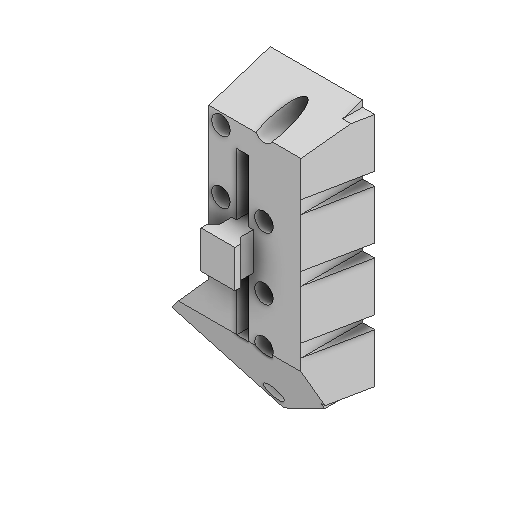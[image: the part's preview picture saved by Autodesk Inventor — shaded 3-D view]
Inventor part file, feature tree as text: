
AUTODESK INVENTOR PART (.ipt)
format: ipt  version: 2025.1 (Build 291241020, 241B)  size: 390,656 bytes
history: native  units: in
note: dims shown in document units (in); Inventor stores cm internally (conversion verified against a paired STEP export)
features: reference x48, other x12, extrude x11, sketch x11, plane x2, chamfer x2, projected_geometry x1
ambient origin geometry x8: Origin, YZ Plane, XZ Plane, XY Plane, X Axis, Y Axis, Z Axis, Center Point
bodies: Solid1 (feature_tree)
feature tree (87):
  extrude  "Extrusion1"  Depth=0.25in TaperAngle=0.0deg
  extrude  "Extrusion2"  Depth=0.14in
  extrude  "Extrusion3"  Depth=0.14in
  plane  "Work Plane1"
  extrude  "Extrusion4"  Depth=0.14in
  extrude  "Extrusion5"  Depth=0.25in TaperAngle=0.0deg
  extrude  "Extrusion6"  Depth=0.3in
  plane  "Work Plane2"
  extrude  "Extrusion7"  Depth=0.3in
  extrude  "Extrusion9"  Depth=0.25in TaperAngle=0.0deg
  extrude  "Extrusion14"  Depth=0.7in
  chamfer  "Chamfer2"  Distance=0.14in
  extrude  "Extrusion15"  Depth=0.25in
  extrude  "Extrusion16"  Depth=0.1in
  chamfer  "Chamfer3"  Distance=0.14in
  sketch  "Sketch1"  dims[d0=0.25in d1=0.0in d2=0.25in d3=0.0in]
  reference  "Reference1"
  reference  "Reference2"
  reference  "Reference3"
  reference  "Reference4"
  reference  "Reference5"
  reference  "Reference6"
  reference  "Reference7"
  reference  "Reference8"
  reference  "Reference9"
  reference  "Reference10"
  reference  "Reference11"
  reference  "Reference12"
  reference  "Reference13"
  reference  "Reference14"
  reference  "Reference15"
  reference  "Reference16"
  reference  "Reference17"
  reference  "Reference18"
  reference  "Reference19"
  reference  "Reference20"
  reference  "Reference21"
  reference  "Reference22"
  reference  "Reference23"
  reference  "Reference24"
  reference  "Reference25"
  reference  "Reference26"
  reference  "Reference27"
  sketch  "Sketch2"  dims[d4=0.7in d5=0.14in d7=0.14in]
  reference  "Reference28"
  reference  "Reference29"
  reference  "Reference30"
  reference  "Reference31"
  reference  "Reference32"
  reference  "Reference33"
  reference  "Reference34"
  reference  "Reference35"
  reference  "Reference36"
  reference  "Reference37"
  reference  "Reference38"
  reference  "Reference39"
  reference  "Reference40"
  reference  "Reference41"
  reference  "Reference42"
  reference  "Reference43"
  sketch  "Sketch3"  dims[d8=0.14in d9=0.14in]
  reference  "Reference44"
  reference  "Reference45"
  reference  "Reference46"
  sketch  "Sketch5"  dims[d10=0.14in d12=0.14in]
  sketch  "Sketch6"  dims[d13=0.35in d14=0.25in d15=0.0in]
  sketch  "Sketch7"  dims[d16=-0.1in d17=0.3in]
  projected_geometry  "Projected Loop1"
  sketch  "Sketch8"  dims[d19=0.3in d20=0.3in]
  sketch  "Sketch10"  dims[d22=0.3in d25=0.25in d26=0.0in]
  reference  "Reference48"
  sketch  "Sketch15"  dims[d27=0.14in d28=0.7in]
  reference  "Reference49"
  sketch  "Sketch16"  dims[d29=0.25in]
  sketch  "Sketch17"  dims[d30=0.3in d31=0.14in d32=0.25in d33=0.3in d34=0.14in d35=0.3in d36=0.3in d37=0.75in d38=0.0in d40=4.25in d41=0.0in d42=0.25in d43=1.4in d44=0.325in d45=6.3125in d46=0.0in d52=0.6in d53=0.0in d75=2.625in d76=0.0in d80=0.1in d81=0.125in d82=45.0deg d83=0.35in d84=0.175in d85=0.3in d86=0.0in d87=0.55in d88=0.1in d89=0.0in d90=0.1in d91=0.125in d92=45.0deg]
  parser-record x1  (decoder bookkeeping rows leaked as tree rows — omitted from the tree; the rows remain in map.json)
  other  "Hand Assem.iam"
  other  "Thumb Base2:1"
  other  "PALM 3:1"
  other  "PALM 2:1"
  other  "PALM 1:1"
  other  "KNUCKLE 1:1"
  other  "KNUCKLE 2:1"
  other  "KNUCKLE 3:1"
  other  "PALM 4:1"
  other  "KNUCKLE 4:1"
  other  "Palm:1"
note: 1 file-system path scrubbed to <path> (originals preserved in map.json)
